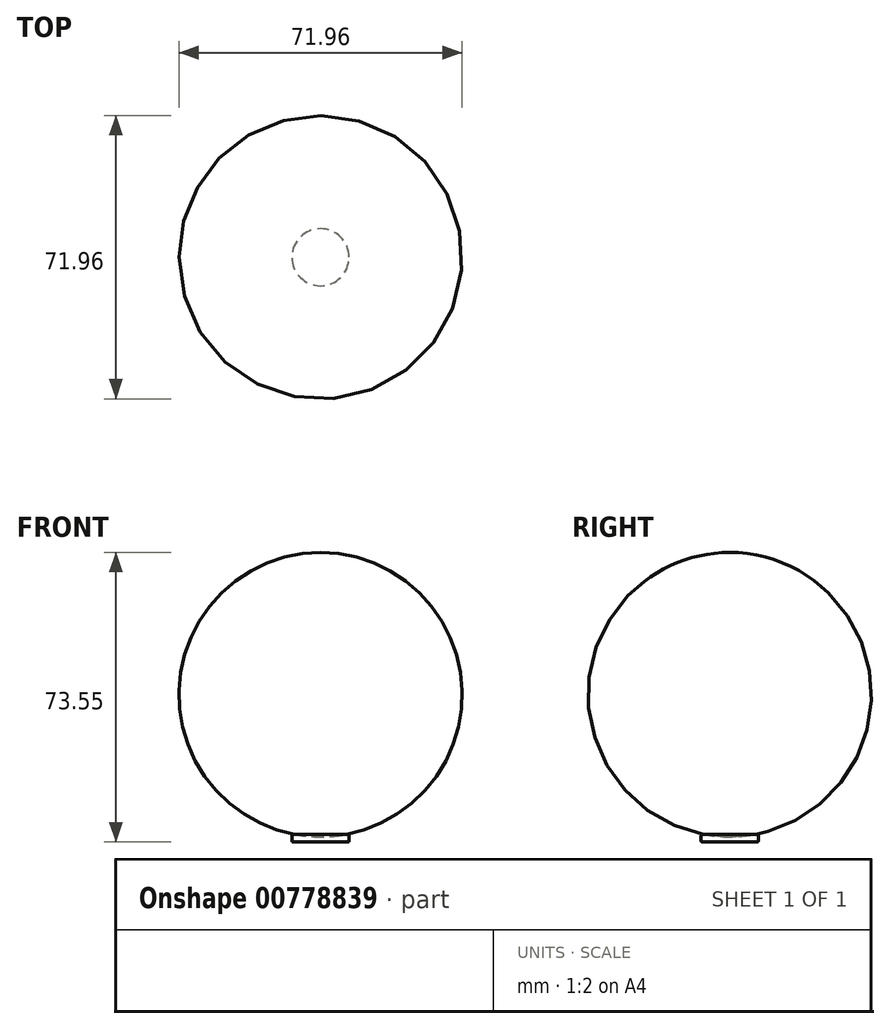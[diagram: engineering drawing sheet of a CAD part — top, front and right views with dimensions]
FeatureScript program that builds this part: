
annotation { "Feature Type Name" : "Feature", "Feature Type Description" : "" }
export const myFeature = defineFeature(function(context is Context, id is Id, definition is map)
    precondition{}
    {
        {
            var Q0;
            Q0=qCreatedBy(makeId("Front.planeOp"),FACE);
            var sketch = newSketch(context, id + "F0", { "sketchPlane" : qUnion([Q0])});
            skLineSegment(sketch, "E0.bottom", {"start": v(-14.7, 4) * mm, "end": v(-7.46, 4) * mm});
            skLineSegment(sketch, "E0.top", {"start": v(-14.7, 2) * mm, "end": v(-7.46, 2) * mm});
            skLineSegment(sketch, "E0.left", {"start": v(-14.7, 4) * mm, "end": v(-14.7, 2) * mm});
            skLineSegment(sketch, "E0.right", {"start": v(-7.46, 4) * mm, "end": v(-7.46, 2) * mm});
            skArc(sketch, "E1", {"start": v(-14.7, 4) * mm, "mid": v(-11.1, 3.47) * mm, "end": v(-7.46, 3.3) * mm});
            skSolve(sketch);
        }
        {
            var Q0;
            {var subQ0=sQuery(id+"F0.wireOp",EDGE,"E0.top");Q0=makeQuery(id+"F0.imprint","IMPRINT",FACE,{"disambiguationData":[TD([[makeQuery(id+"F0.imprint","IMPRINT",EDGE,{"derivedFrom":subQ0}),1.0]])]});}
            var Q1;
            Q1=sQuery(id+"F0.wireOp",EDGE,"E0.right");
            revolve(context, id + "F1", {"surfaceOperationType" : NewSurfaceOperationType.NEW, "entities" : qUnion([Q0]), "axis" : qUnion([Q1]), "revolveType" : RevolveType.FULL});
        }
        {
            var Q0;
            Q0=makeQuery(id+"F1.opRevolve","SWEPT_EDGE",EDGE,{"disambiguationData":[OSD([sQuery(id+"F0.wireOp",EDGE,"E0.top"),sQuery(id+"F0.wireOp",EDGE,"E0.left")])]});
            fillet(context, id + "F2", {"entities" : qUnion([Q0]), "radius" : 0.2 * mm, "tangentPropagation" : true, "allowEdgeOverflow" : false});
        }
        {
            var Q0;
            Q0=makeQuery(id+"F1.opRevolve","SWEPT_EDGE",EDGE,{"disambiguationData":[OSD([sQuery(id+"F0.wireOp",EDGE,"E0.bottom"),sQuery(id+"F0.wireOp",EDGE,"E0.left"),sQuery(id+"F0.wireOp",EDGE,"E1")])]});
            fillet(context, id + "F3", {"entities" : qUnion([Q0]), "radius" : 0.3 * mm, "tangentPropagation" : true, "allowEdgeOverflow" : false});
        }
    });
